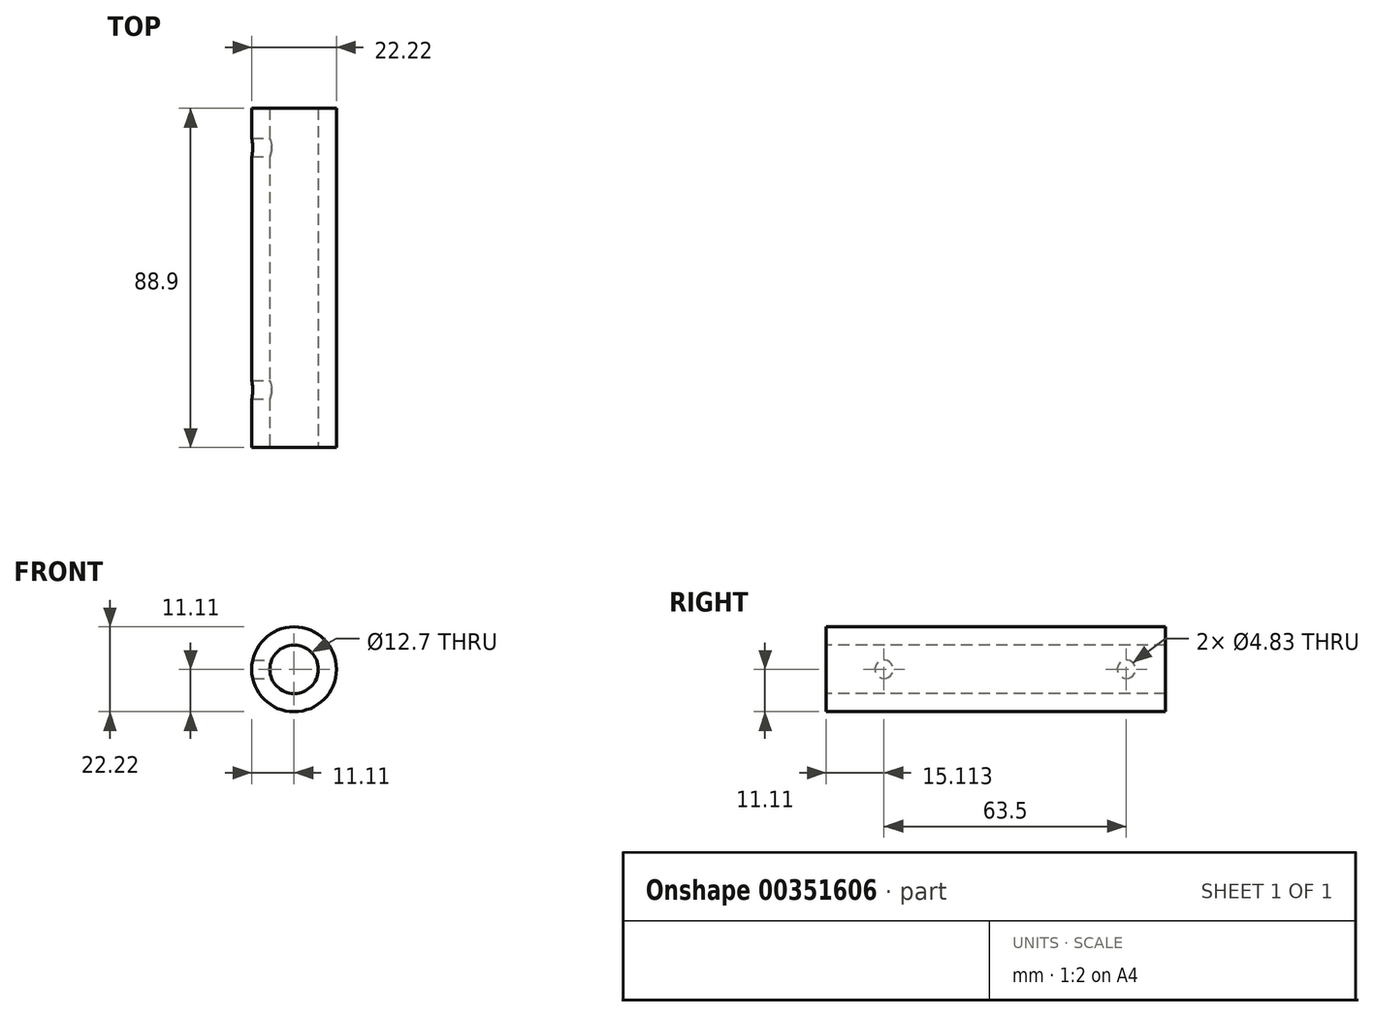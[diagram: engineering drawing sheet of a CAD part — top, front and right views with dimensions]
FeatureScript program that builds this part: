
annotation { "Feature Type Name" : "Feature", "Feature Type Description" : "" }
export const myFeature = defineFeature(function(context is Context, id is Id, definition is map)
    precondition{}
    {
        {
            var Q0;
            Q0=qCreatedBy(makeId("Front.planeOp"),FACE);
            var sketch = newSketch(context, id + "F0", { "sketchPlane" : qUnion([Q0])});
            skCircle(sketch, "E0", {"center": v(0, 0) * mm, "radius": 11.11 * mm});
            skSolve(sketch);
        }
        {
            var Q0;
            Q0=makeQuery(id+"F0.imprint","IMPRINT",FACE,{"disambiguationData":[TD([[makeQuery(id+"F0.imprint","IMPRINT",EDGE,{"derivedFrom":sQuery(id+"F0.wireOp",EDGE,"E0")}),1.0]])]});
            extrude(context, id + "F1", {"entities" : qUnion([Q0]), "depth" : 88.9 * mm, "symmetric" : true});
        }
        {
            var Q0;
            Q0=makeQuery(id+"F1.opExtrude","CAP_FACE",FACE,{"disambiguationData":[OSD([sQuery(id+"F0.wireOp",EDGE,"E0")])],"isStart":false});
            var sketch = newSketch(context, id + "F2", { "sketchPlane" : qUnion([Q0])});
            skCircle(sketch, "E1", {"center": v(0, 0) * mm, "radius": 6.35 * mm});
            skSolve(sketch);
        }
        {
            var Q0;
            Q0=makeQuery(id+"F2.imprint","IMPRINT",FACE,{"disambiguationData":[TD([[makeQuery(id+"F2.imprint","IMPRINT",EDGE,{"derivedFrom":sQuery(id+"F2.wireOp",EDGE,"E1")}),1.0]])]});
            extrude(context, id + "F3", {"entities" : qUnion([Q0]), "operationType" : NewBodyOperationType.REMOVE, "oppositeDirection" : true, "depth" : 88.9 * mm});
        }
        {
            var Q0;
            Q0=qCreatedBy(makeId("Right.planeOp"),FACE);
            var sketch = newSketch(context, id + "F4", { "sketchPlane" : qUnion([Q0])});
            skCircle(sketch, "E2", {"center": v(-29.34, 0) * mm, "radius": 2.41 * mm});
            skSolve(sketch);
        }
        {
            var Q0;
            Q0 = qSketchRegion(id + "F4", true);
            extrude(context, id + "F5", {"entities" : qUnion([Q0]), "operationType" : NewBodyOperationType.REMOVE, "oppositeDirection" : true, "depth" : 25.4 * mm});
        }
        {
            var Q0;
            Q0=qCreatedBy(makeId("Right.planeOp"),FACE);
            var sketch = newSketch(context, id + "F6", { "sketchPlane" : qUnion([Q0])});
            skCircle(sketch, "E3", {"center": v(34.16, 0) * mm, "radius": 2.41 * mm});
            skSolve(sketch);
        }
        {
            var Q0;
            Q0 = qSketchRegion(id + "F6", true);
            extrude(context, id + "F7", {"entities" : qUnion([Q0]), "operationType" : NewBodyOperationType.REMOVE, "oppositeDirection" : true, "depth" : 25.4 * mm});
        }
    });
